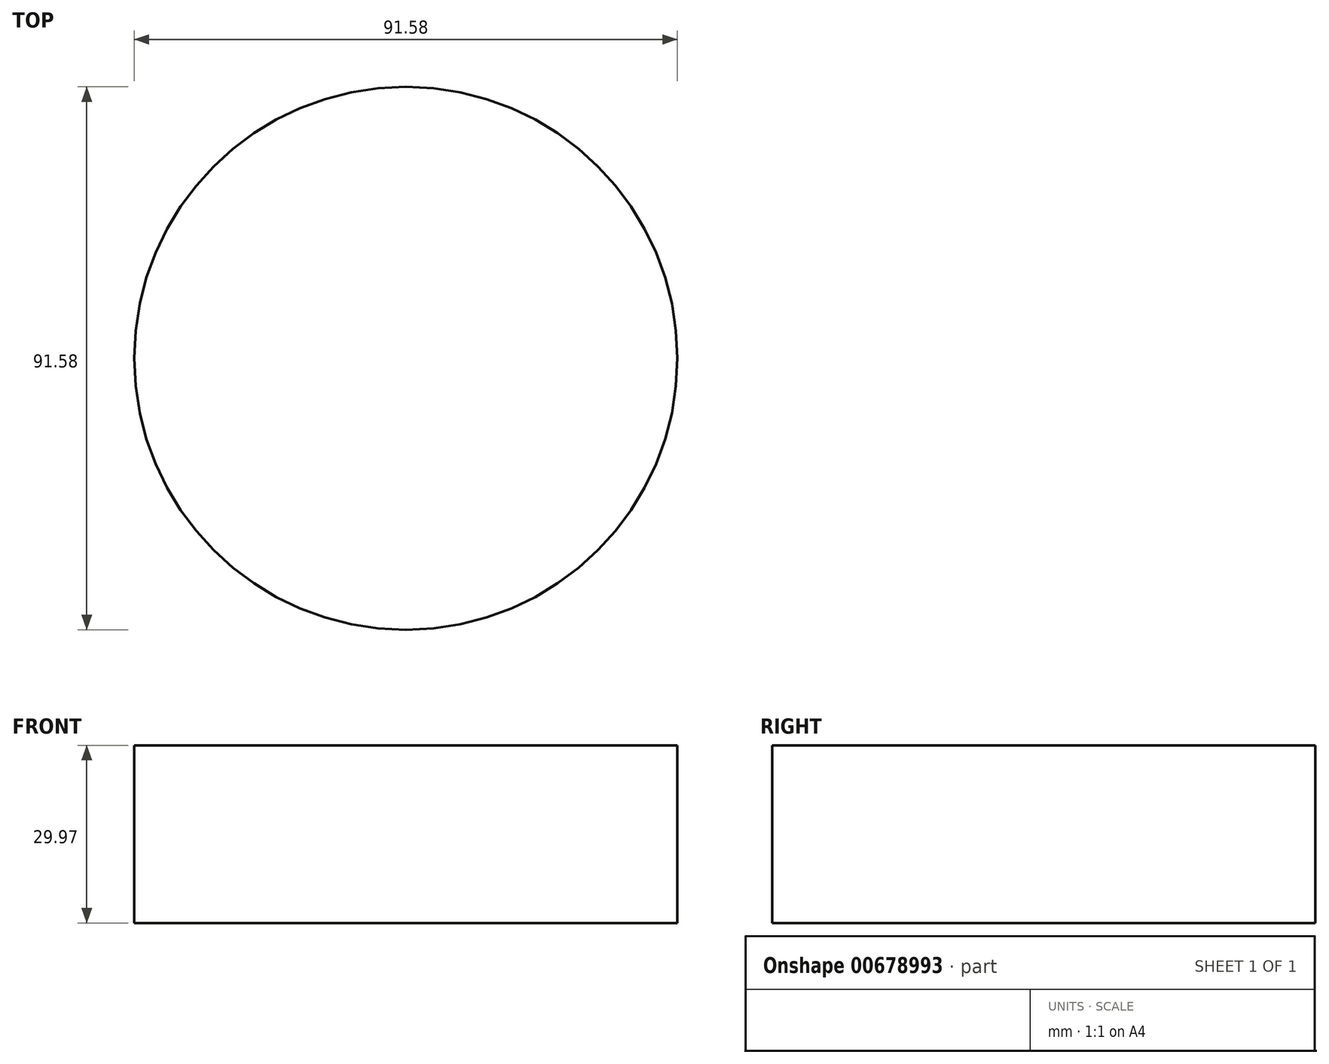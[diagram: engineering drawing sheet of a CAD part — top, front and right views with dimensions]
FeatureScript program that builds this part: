
annotation { "Feature Type Name" : "Feature", "Feature Type Description" : "" }
export const myFeature = defineFeature(function(context is Context, id is Id, definition is map)
    precondition{}
    {
        {
            var Q0;
            Q0=qCreatedBy(makeId("Top.planeOp"),FACE);
            var sketch = newSketch(context, id + "F0", { "sketchPlane" : qUnion([Q0])});
            skLineSegment(sketch, "E0.bottom", {"start": v(-43.73, 0) * mm, "end": v(30.1, 0) * mm});
            skLineSegment(sketch, "E0.top", {"start": v(-50.08, -49.78) * mm, "end": v(30.1, -49.78) * mm});
            skLineSegment(sketch, "E0.left", {"start": v(-50.08, -6.35) * mm, "end": v(-50.08, -49.78) * mm});
            skLineSegment(sketch, "E0.right", {"start": v(30.1, 0) * mm, "end": v(30.1, -49.78) * mm});
            skPoint(sketch, "E1.visualSharp", {"position": v(-50.08, 0) * mm});
            skArc(sketch, "E1.filletArc", {"start": v(-43.73, 0) * mm, "mid": v(-48.22, -1.86) * mm, "end": v(-50.08, -6.35) * mm});
            skCircle(sketch, "E2", {"center": v(-66.13, 34.47) * mm, "radius": 45.8 * mm});
            skSolve(sketch);
        }
        {
            var Q0;
            {var subQ0=sQuery(id+"F0.wireOp",EDGE,"E1.filletArc");Q0=makeQuery(id+"F0.imprint","IMPRINT",FACE,{"disambiguationData":[TD([[makeQuery(id+"F0.imprint","IMPRINT",EDGE,{"derivedFrom":subQ0}),-1.0]])]});}
            var Q1;
            {var subQ0=sQuery(id+"F0.wireOp",EDGE,"E1.filletArc");Q1=makeQuery(id+"F0.imprint","IMPRINT",FACE,{"disambiguationData":[TD([[makeQuery(id+"F0.imprint","IMPRINT",EDGE,{"derivedFrom":subQ0}),1.0]])]});}
            extrude(context, id + "F1", {"entities" : qUnion([Q0, Q1]), "depth" : 29.97 * mm, "offsetDistance" : 25.4 * mm});
        }
    });
